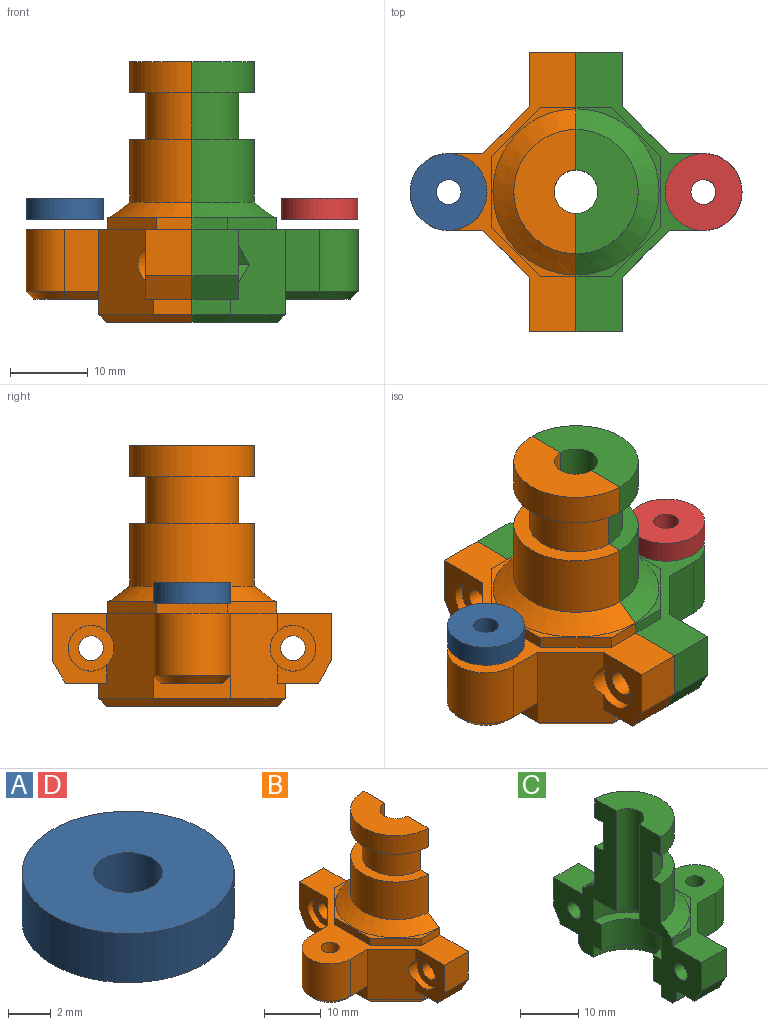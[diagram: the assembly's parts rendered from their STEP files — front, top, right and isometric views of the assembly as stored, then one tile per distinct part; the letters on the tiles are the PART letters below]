
ASSEMBLY  parts=4 mates=1
PART A: 4 faces, bbox 9.9x9.9x2.8 mm
  f0: plane 9.9x9.9mm, normal (0,0,1), area 68.9mm2, adj f2,f3
  f1: plane 9.9x9.9mm, normal (0,0,-1), area 68.9mm2, adj f2,f3
  f2: cylinder r=4.95mm len=9.9mm, axis (0,0,-1), area 87.1mm2, adj f0,f1
  f3: cylinder r=1.6mm len=3.2mm, axis (0,0,-1), area 28.1mm2, adj f0,f1
PART B: 58 faces, bbox 21.4x36x33.6 mm
  f0: plane 9x7.03mm, normal (-1,0,0), area 36mm2, adj f12,f13,f15,f19,f32,f49
  f1: plane 6x5.33mm, normal (0,0,-1), area 26.3mm2, adj f16,f20,f36,f37,f40
  f2: cylinder r=8mm len=16mm, axis (0,0,-1), area 203.6mm2, adj f8,f11,f39,f40
  f3: plane 4.52x1.5mm, normal (0,1,0), area 6.8mm2, adj f5,f12,f29,f40
  f4: plane 4.52x1.5mm, normal (0,-1,0), area 6.8mm2, adj f5,f12,f31,f39
  f5: plane 21.8x10.9mm, normal (0,0,1), area 17mm2, adj f3,f4,f11,f29,f30,f31,f39,f40
  f6: cylinder r=6mm len=12mm, axis (0,0,-1), area 113.1mm2, adj f7,f8,f39,f40
  f7: plane 16x8mm, normal (0,0,-1), area 44mm2, adj f6,f10,f39,f40
  f8: plane 16x8mm, normal (0,0,1), area 44mm2, adj f2,f6,f39,f40
  f9: plane 16x8mm, normal (0,0,1), area 88.2mm2, adj f10,f27,f39,f40
  f10: cylinder r=8mm len=16mm, axis (0,0,-1), area 100.5mm2, adj f7,f9,f39,f40
  f11: cone r=8mm half-angle=53.5deg, axis (0,0,-1), area 98.7mm2, adj f2,f5,f39,f40
  f12: plane 36x21.37mm, normal (0,0,1), area 189.3mm2, adj f0,f3,f4,f13,f14,f29,f30,f31
  f13: plane 6x6mm, normal (0,-1,0), area 36mm2, adj f0,f12,f19,f39
  f14: plane 6.06x6mm, normal (0,1,0), area 36.3mm2, adj f12,f20,f37,f40
  f15: plane 6x5.3mm, normal (0,0,-1), area 26.1mm2, adj f0,f18,f19,f32,f39
  f16: plane 4.97x2mm, normal (0,1,0), area 9.9mm2, adj f1,f36,f40,f57
  f17: plane 22x11mm, normal (0,0,-1), area 92.3mm2, adj f21,f39,f40,f53,f54,f55,f56,f57
  f18: plane 4.97x2mm, normal (0,-1,0), area 9.9mm2, adj f15,f32,f39,f53
  f19: plane 6x3mm, normal (0,-0.87,-0.5), area 20.8mm2, adj f0,f13,f15,f39
  f20: plane 6x2.94mm, normal (0,0.87,-0.5), area 20.4mm2, adj f1,f14,f37,f40
  f21: cylinder r=8.3mm len=16.6mm, axis (0,0,-1), area 62.6mm2, adj f17,f25,f39,f40
  f22: plane 16.6x8.3mm, normal (0,0,-1), area 95.9mm2, adj f26,f27,f39,f40
  f23: cylinder r=6.3mm len=12.6mm, axis (0,0,-1), area 106.9mm2, adj f24,f25,f39,f40
  f24: plane 16.6x8.3mm, normal (0,0,1), area 45.9mm2, adj f23,f26,f39,f40
  f25: plane 16.6x8.3mm, normal (0,0,-1), area 45.9mm2, adj f21,f23,f39,f40
  f26: cylinder r=8.3mm len=16.6mm, axis (0,0,-1), area 119.9mm2, adj f22,f24,f39,f40
  f27: cylinder r=2.8mm len=21.2mm, axis (0,0,1), area 186.5mm2, adj f9,f22,f39,f40
  f28: plane 8.37x7.94mm, normal (0,0,-1), area 32.4mm2, adj f38,f43,f50,f51,f52
  f29: plane 6.39x6.39mm, normal (-0.71,0.71,0), area 13.5mm2, adj f3,f5,f12,f30
  f30: plane 9.03x1.5mm, normal (-1,0,0), area 13.5mm2, adj f5,f12,f29,f31
  f31: plane 6.39x6.39mm, normal (-0.71,-0.71,0), area 13.5mm2, adj f4,f5,f12,f30
  f32: plane 11x7.03mm, normal (-0.71,-0.71,0), area 92.4mm2, adj f0,f12,f15,f18,f33,f38,f49,f54
  f33: plane 8x4.4mm, normal (0,-1,0), area 35.2mm2, adj f12,f32,f34,f52
  f34: cylinder r=4.97mm len=9.94mm, axis (0,0,1), area 124.9mm2, adj f12,f33,f35,f51
  f35: plane 8x4.4mm, normal (0,1,0), area 35.2mm2, adj f12,f34,f36,f50
  f36: plane 11x7.03mm, normal (-0.71,0.71,0), area 92.4mm2, adj f1,f12,f16,f35,f37,f38,f46,f56
  f37: plane 9x7.03mm, normal (-1,0,0), area 36.1mm2, adj f1,f12,f14,f20,f36,f46
  f38: plane 9.94x3mm, normal (-1,0,0), area 20.9mm2, adj f28,f32,f36,f50,f52,f55
  f39: plane 33.6x15.2mm, normal (1,0,0), area 203.2mm2, adj f2,f4,f5,f6,f7,f8,f9,f10
  f40: plane 33.6x15.2mm, normal (1,0,0), area 203.3mm2, adj f1,f2,f3,f5,f6,f7,f8,f9
  f41: cylinder r=1.6mm len=7.8mm, axis (0,0,-1), area 78.4mm2, adj f12,f42
  f42: plane 5.9x5.9mm, normal (0,0,-1), area 19.3mm2, adj f41,f43
  f43: cylinder r=2.95mm len=5.9mm, axis (0,0,-1), area 22.2mm2, adj f28,f42
  f44: cylinder r=1.6mm len=4.8mm, axis (-1,0,0), area 48.3mm2, adj f40,f45
  f45: plane 5.9x5.9mm, normal (-1,0,0), area 19.3mm2, adj f44,f46
  f46: cylinder r=2.95mm len=5.9mm, axis (-1,0,0), area 25.2mm2, adj f36,f37,f45
  f47: cylinder r=1.6mm len=4.8mm, axis (-1,0,0), area 48.3mm2, adj f39,f48
  f48: plane 5.9x5.9mm, normal (-1,0,0), area 19.3mm2, adj f47,f49
  f49: cylinder r=2.95mm len=5.9mm, axis (-1,0,0), area 25.2mm2, adj f0,f32,f48
  f50: plane 4.4x1mm, normal (0,0.71,-0.71), area 6.2mm2, adj f28,f35,f38,f51
  f51: cone r=3.97mm half-angle=45deg, axis (0,0,1), area 19.9mm2, adj f28,f34,f50,f52
  f52: plane 4.4x1mm, normal (0,-0.71,-0.71), area 6.2mm2, adj f28,f33,f38,f51
  f53: plane 4.97x1mm, normal (0,-0.71,-0.71), area 6.7mm2, adj f17,f18,f39,f54
  f54: plane 7.44x7.44mm, normal (-0.5,-0.5,-0.71), area 13.5mm2, adj f17,f32,f53,f55
  f55: plane 9.94x1mm, normal (-0.71,0,-0.71), area 13.5mm2, adj f17,f38,f54,f56
  f56: plane 7.44x7.44mm, normal (-0.5,0.5,-0.71), area 13.5mm2, adj f17,f36,f55,f57
  f57: plane 4.97x1mm, normal (0,0.71,-0.71), area 6.7mm2, adj f16,f17,f40,f56
PART C: 68 faces, bbox 21.4x36x33.6 mm
  f0: plane 11x7.03mm, normal (0.71,-0.71,0), area 91.6mm2, adj f1,f10,f11,f27,f30,f32,f48,f49
  f1: plane 9x7.03mm, normal (1,0,0), area 33.8mm2, adj f0,f19,f30,f31,f32,f47,f48,f49
  f2: cylinder r=1.6mm len=4mm, axis (-1,0,0), area 40.2mm2, adj f42,f53
  f3: cylinder r=1.6mm len=4mm, axis (-1,0,0), area 40.2mm2, adj f41,f46
  f4: plane 8.37x7.94mm, normal (0,0,-1), area 32.4mm2, adj f11,f45,f60,f61,f62
  f5: plane 6.39x6.39mm, normal (0.71,-0.71,0), area 13.5mm2, adj f6,f15,f32,f37
  f6: plane 9.03x1.5mm, normal (1,0,0), area 13.5mm2, adj f5,f7,f15,f32
  f7: plane 6.39x6.39mm, normal (0.71,0.71,0), area 13.5mm2, adj f6,f15,f32,f38
  f8: plane 8x4.4mm, normal (0,1,0), area 35.2mm2, adj f9,f12,f32,f60
  f9: cylinder r=4.97mm len=9.94mm, axis (0,0,1), area 124.9mm2, adj f8,f10,f32,f61
  f10: plane 8x4.4mm, normal (0,-1,0), area 35.2mm2, adj f0,f9,f32,f62
  f11: plane 9.94x3mm, normal (1,0,0), area 20.9mm2, adj f0,f4,f12,f60,f62,f65
  f12: plane 11x7.03mm, normal (0.71,0.71,0), area 91.6mm2, adj f8,f11,f13,f29,f32,f40,f54,f59
  f13: plane 9x7.03mm, normal (1,0,0), area 33.9mm2, adj f12,f17,f18,f32,f40,f54,f55,f56
  f14: cone r=8mm half-angle=53.5deg, axis (0,0,-1), area 98.7mm2, adj f15,f39,f41,f42
  f15: plane 21.8x10.9mm, normal (0,0,1), area 17mm2, adj f5,f6,f7,f14,f37,f38,f41,f42
  f16: plane 16x8mm, normal (0,0,1), area 44mm2, adj f36,f39,f41,f42
  f17: plane 6x2.94mm, normal (0,0.87,-0.5), area 20.4mm2, adj f13,f18,f40,f42
  f18: plane 6.06x6mm, normal (0,1,0), area 36.3mm2, adj f13,f17,f32,f42
  f19: plane 6x3mm, normal (0,-0.87,-0.5), area 20.8mm2, adj f1,f30,f31,f41
  f20: cylinder r=2.8mm len=21.2mm, axis (0,0,1), area 186.5mm2, adj f25,f34,f41,f42
  f21: plane 16.6x8.3mm, normal (0,0,-1), area 45.9mm2, adj f24,f26,f41,f42
  f22: cylinder r=8.3mm len=16.6mm, axis (0,0,-1), area 119.9mm2, adj f23,f25,f41,f42
  f23: plane 16.6x8.3mm, normal (0,0,1), area 45.9mm2, adj f22,f24,f41,f42
  f24: cylinder r=6.3mm len=12.6mm, axis (0,0,-1), area 106.9mm2, adj f21,f23,f41,f42
  f25: plane 16.6x8.3mm, normal (0,0,-1), area 95.9mm2, adj f20,f22,f41,f42
  f26: cylinder r=8.3mm len=16.6mm, axis (0,0,-1), area 62.6mm2, adj f21,f28,f41,f42
  f27: plane 4.97x2mm, normal (0,-1,0), area 9.9mm2, adj f0,f30,f41,f63
  f28: plane 22x11mm, normal (0,0,-1), area 92.3mm2, adj f26,f41,f42,f63,f64,f65,f66,f67
  f29: plane 4.97x2mm, normal (0,1,0), area 9.9mm2, adj f12,f40,f42,f67
  f30: plane 6x5.3mm, normal (0,0,-1), area 26.1mm2, adj f0,f1,f19,f27,f41
  f31: plane 6x6mm, normal (0,-1,0), area 36mm2, adj f1,f19,f32,f41
  f32: plane 36x21.37mm, normal (0,0,1), area 189.3mm2, adj f0,f1,f5,f6,f7,f8,f9,f10
  f33: cylinder r=8mm len=16mm, axis (0,0,-1), area 100.5mm2, adj f34,f35,f41,f42
  f34: plane 16x8mm, normal (0,0,1), area 88.2mm2, adj f20,f33,f41,f42
  f35: plane 16x8mm, normal (0,0,-1), area 44mm2, adj f33,f36,f41,f42
  f36: cylinder r=6mm len=12mm, axis (0,0,-1), area 113.1mm2, adj f16,f35,f41,f42
  f37: plane 4.52x1.5mm, normal (0,-1,0), area 6.8mm2, adj f5,f15,f32,f41
  f38: plane 4.52x1.5mm, normal (0,1,0), area 6.8mm2, adj f7,f15,f32,f42
  f39: cylinder r=8mm len=16mm, axis (0,0,-1), area 203.6mm2, adj f14,f16,f41,f42
  f40: plane 6x5.33mm, normal (0,0,-1), area 26.3mm2, adj f12,f13,f17,f29,f42
  f41: plane 33.6x15.2mm, normal (-1,0,0), area 203.2mm2, adj f3,f14,f15,f16,f19,f20,f21,f22
  f42: plane 33.6x15.2mm, normal (-1,0,0), area 203.3mm2, adj f2,f14,f15,f16,f17,f18,f20,f21
  f43: cylinder r=1.6mm len=7.8mm, axis (0,0,-1), area 78.4mm2, adj f32,f44
  f44: plane 5.9x5.9mm, normal (0,0,-1), area 19.3mm2, adj f43,f45
  f45: cylinder r=2.95mm len=5.9mm, axis (0,0,-1), area 22.2mm2, adj f4,f44
  f46: plane 6.81x5.9mm, normal (1,0,0), area 22.1mm2, adj f3,f47,f48,f49,f50,f51,f52
  f47: plane 3.41x2mm, normal (0,0,-1), area 6.8mm2, adj f1,f46,f48,f51
  f48: plane 3.38x2.95mm, normal (0,-0.87,-0.5), area 8.7mm2, adj f0,f1,f46,f47,f49
  f49: plane 3.38x2.95mm, normal (0,-0.87,0.5), area 8.7mm2, adj f0,f1,f46,f48,f50
  f50: plane 3.41x2mm, normal (0,0,1), area 6.8mm2, adj f1,f46,f49,f52
  f51: plane 2.95x2mm, normal (0,0.87,-0.5), area 6.8mm2, adj f1,f46,f47,f52
  f52: plane 2.95x2mm, normal (0,0.87,0.5), area 6.8mm2, adj f1,f46,f50,f51
  f53: plane 6.81x5.9mm, normal (1,0,0), area 22.1mm2, adj f2,f54,f55,f56,f57,f58,f59
  f54: plane 3.38x2.95mm, normal (0,0.87,-0.5), area 8.7mm2, adj f12,f13,f53,f55,f59
  f55: plane 3.41x2mm, normal (0,0,-1), area 6.8mm2, adj f13,f53,f54,f56
  f56: plane 2.95x2mm, normal (0,-0.87,-0.5), area 6.8mm2, adj f13,f53,f55,f57
  f57: plane 2.95x2mm, normal (0,-0.87,0.5), area 6.8mm2, adj f13,f53,f56,f58
  f58: plane 3.41x2mm, normal (0,0,1), area 6.8mm2, adj f13,f53,f57,f59
  f59: plane 3.38x2.95mm, normal (0,0.87,0.5), area 8.7mm2, adj f12,f13,f53,f54,f58
  f60: plane 4.4x1mm, normal (0,0.71,-0.71), area 6.2mm2, adj f4,f8,f11,f61
  f61: cone r=4.97mm half-angle=45deg, axis (0,0,1), area 19.9mm2, adj f4,f9,f60,f62
  f62: plane 4.4x1mm, normal (0,-0.71,-0.71), area 6.2mm2, adj f4,f10,f11,f61
  f63: plane 4.97x1mm, normal (0,-0.71,-0.71), area 6.7mm2, adj f27,f28,f41,f64
  f64: plane 7.44x7.44mm, normal (0.5,-0.5,-0.71), area 13.5mm2, adj f0,f28,f63,f65
  f65: plane 9.94x1mm, normal (0.71,0,-0.71), area 13.5mm2, adj f11,f28,f64,f66
  f66: plane 7.44x7.44mm, normal (0.5,0.5,-0.71), area 13.5mm2, adj f12,f28,f65,f67
  f67: plane 4.97x1mm, normal (0,0.71,-0.71), area 6.7mm2, adj f28,f29,f42,f66
PART D: same geometry as A
PLACE A rot(axis=(-1,0,0),180deg) t=(64,77.2,-6)mm
PLACE B t=(64,1.22,0)mm
PLACE C t=(64,1.22,0)mm
PLACE D rot(axis=(-1,0,0),180deg) t=(96.8,77.2,-6)mm
MATE fastened C.f2 <-> B.f44  axis (-1,0,0) through (32,52.22,-9.5)mm
